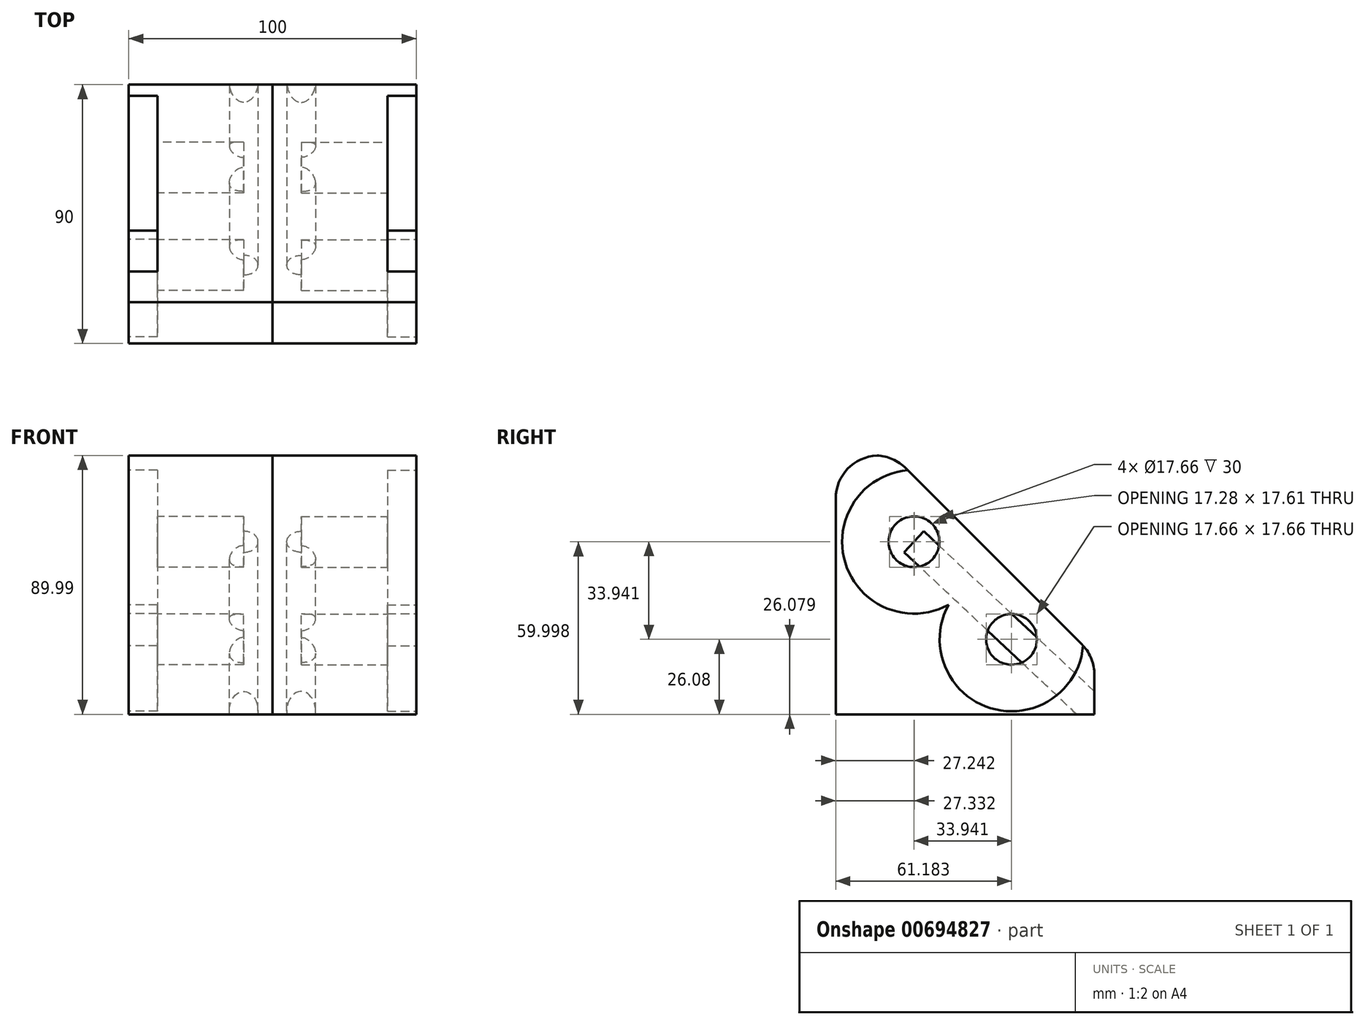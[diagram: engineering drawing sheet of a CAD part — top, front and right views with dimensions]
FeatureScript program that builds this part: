
annotation { "Feature Type Name" : "Feature", "Feature Type Description" : "" }
export const myFeature = defineFeature(function(context is Context, id is Id, definition is map)
    precondition{}
    {
        {
            var Q0;
            Q0=qCreatedBy(makeId("Right.planeOp"),FACE);
            var sketch = newSketch(context, id + "F0", { "sketchPlane" : qUnion([Q0])});
            skLineSegment(sketch, "E0.bottom", {"start": v(45, 45) * mm, "end": v(-45, 45) * mm});
            skLineSegment(sketch, "E0.top", {"start": v(45, -45) * mm, "end": v(-45, -45) * mm});
            skLineSegment(sketch, "E0.left", {"start": v(45, 45) * mm, "end": v(45, -45) * mm});
            skLineSegment(sketch, "E0.right", {"start": v(-45, 45) * mm, "end": v(-45, -45) * mm});
            skPoint(sketch, "E0.middle", {"position": v(0, 0) * mm});
            skCircle(sketch, "E1", {"center": v(-17.76, 15.02) * mm, "radius": 8.83 * mm});
            skCircle(sketch, "E2", {"center": v(16.18, -18.92) * mm, "radius": 8.83 * mm});
            skLineSegment(sketch, "E3", {"start": v(-17.76, 15.02) * mm, "end": v(-17.76, -18.92) * mm, "construction": true});
            skLineSegment(sketch, "E4", {"start": v(-17.76, -18.92) * mm, "end": v(16.18, -18.92) * mm, "construction": true});
            skLineSegment(sketch, "E5", {"start": v(-17.76, 15.02) * mm, "end": v(16.18, -18.92) * mm, "construction": true});
            skCircle(sketch, "E6", {"center": v(-17.76, 15.02) * mm, "radius": 25 * mm});
            skCircle(sketch, "E7", {"center": v(16.18, -18.92) * mm, "radius": 25 * mm});
            skSolve(sketch);
        }
        {
            var Q0;
            Q0=makeQuery(id+"F0.imprint","IMPRINT",FACE,{"disambiguationData":[TD([[makeQuery(id+"F0.imprint","IMPRINT",EDGE,{"derivedFrom":sQuery(id+"F0.wireOp",EDGE,"E0.bottom")}),1.0]])]});
            var Q1;
            Q1=makeQuery(id+"F0.imprint","IMPRINT",FACE,{"disambiguationData":[TD([[makeQuery(id+"F0.imprint","IMPRINT",EDGE,{"derivedFrom":sQuery(id+"F0.wireOp",EDGE,"E2")}),-1.0]])]});
            var Q2;
            Q2=makeQuery(id+"F0.imprint","IMPRINT",FACE,{"disambiguationData":[TD([[makeQuery(id+"F0.imprint","IMPRINT",EDGE,{"derivedFrom":sQuery(id+"F0.wireOp",EDGE,"E1")}),-1.0]])]});
            var Q3;
            {var subQ0=sQuery(id+"F0.wireOp",EDGE,"E7");var subQ1=sQuery(id+"F0.wireOp",EDGE,"E6");var subQ2=makeQuery(id+"F0.imprint","INTERSECT",VERTEX,{"disambiguationData":[OD(0.0)],"derivedFrom":[subQ1,subQ0]});Q3=makeQuery(id+"F0.imprint","IMPRINT",FACE,{"disambiguationData":[TD([[makeQuery(id+"F0.imprint","IMPRINT",EDGE,{"disambiguationData":[TD([[subQ2,-1.0]])],"derivedFrom":subQ1}),1.0]])]});}
            extrude(context, id + "F1", {"entities" : qUnion([Q0, Q1, Q2, Q3]), "depth" : 50 * mm, "offsetDistance" : 25 * mm});
        }
        {
            var Q0;
            Q0=makeQuery(id+"F1.opExtrude","SWEPT_EDGE",EDGE,{"disambiguationData":[OSD([sQuery(id+"F0.wireOp",EDGE,"E0.bottom"),sQuery(id+"F0.wireOp",EDGE,"E0.left")])]});
            chamfer(context, id + "F2", {"entities" : qUnion([Q0]), "width" : 70 * mm, "tangentPropagation" : true});
        }
        {
            var Q0;
            {var subQ0=sQuery(id+"F0.wireOp",EDGE,"E0.left");Q0=makeQuery(id+"F2.opChamfer","BLEND_EDGE",EDGE,{"blendedFrom":[makeQuery(id+"F1.opExtrude","SWEPT_EDGE",EDGE,{"disambiguationData":[OSD([sQuery(id+"F0.wireOp",EDGE,"E0.bottom"),subQ0])]}),makeQuery(id+"F1.opExtrude","SWEPT_FACE",FACE,{"disambiguationData":[OSD([subQ0])]})],"blendedInto":[makeQuery(id+"F1.opExtrude","SWEPT_FACE",FACE,{"disambiguationData":[OSD([subQ0])]})]});}
            var Q1;
            {var subQ0=sQuery(id+"F0.wireOp",EDGE,"E0.bottom");Q1=makeQuery(id+"F2.opChamfer","BLEND_EDGE",EDGE,{"blendedFrom":[makeQuery(id+"F1.opExtrude","SWEPT_EDGE",EDGE,{"disambiguationData":[OSD([subQ0,sQuery(id+"F0.wireOp",EDGE,"E0.left")])]}),makeQuery(id+"F1.opExtrude","SWEPT_FACE",FACE,{"disambiguationData":[OSD([subQ0])]})],"blendedInto":[makeQuery(id+"F1.opExtrude","SWEPT_FACE",FACE,{"disambiguationData":[OSD([subQ0])]})]});}
            var Q2;
            Q2=makeQuery(id+"F1.opExtrude","SWEPT_EDGE",EDGE,{"disambiguationData":[OSD([sQuery(id+"F0.wireOp",EDGE,"E0.bottom"),sQuery(id+"F0.wireOp",EDGE,"E0.right")])]});
            fillet(context, id + "F3", {"entities" : qUnion([Q0, Q1, Q2]), "radius" : 15 * mm, "tangentPropagation" : true, "allowEdgeOverflow" : false});
        }
        {
            var Q0;
            Q0=makeQuery(id+"F0.imprint","IMPRINT",FACE,{"disambiguationData":[TD([[makeQuery(id+"F0.imprint","IMPRINT",EDGE,{"derivedFrom":sQuery(id+"F0.wireOp",EDGE,"E1")}),-1.0]])]});
            var Q1;
            Q1=makeQuery(id+"F0.imprint","IMPRINT",FACE,{"disambiguationData":[TD([[makeQuery(id+"F0.imprint","IMPRINT",EDGE,{"derivedFrom":sQuery(id+"F0.wireOp",EDGE,"E2")}),-1.0]])]});
            var Q2;
            {var subQ0=sQuery(id+"F0.wireOp",EDGE,"E7");var subQ1=sQuery(id+"F0.wireOp",EDGE,"E6");var subQ2=makeQuery(id+"F0.imprint","INTERSECT",VERTEX,{"disambiguationData":[OD(0.0)],"derivedFrom":[subQ1,subQ0]});Q2=makeQuery(id+"F0.imprint","IMPRINT",FACE,{"disambiguationData":[TD([[makeQuery(id+"F0.imprint","IMPRINT",EDGE,{"disambiguationData":[TD([[subQ2,-1.0]])],"derivedFrom":subQ1}),1.0]])]});}
            extrude(context, id + "F4", {"entities" : qUnion([Q0, Q1, Q2]), "operationType" : NewBodyOperationType.REMOVE, "depth" : 10 * mm, "offsetDistance" : 25 * mm});
        }
        {
            var Q0;
            Q0=makeQuery(id+"F0.imprint","IMPRINT",FACE,{"disambiguationData":[TD([[makeQuery(id+"F0.imprint","IMPRINT",EDGE,{"derivedFrom":sQuery(id+"F0.wireOp",EDGE,"E0.bottom")}),1.0]])]});
            var sketch = newSketch(context, id + "F5", { "sketchPlane" : qUnion([Q0])});
            skPoint(sketch, "E8.0", {"position": v(10.58, 9.42) * mm});
            skArc(sketch, "E9.0.0", {"start": v(14.01, 5.99) * mm, "mid": v(8.93, 5) * mm, "end": v(4.16, 3) * mm});
            skArc(sketch, "E9.0.1", {"start": v(4.16, 3) * mm, "mid": v(6.17, 7.77) * mm, "end": v(7.15, 12.85) * mm});
            skLineSegment(sketch, "E9.0.2", {"start": v(7.15, 12.85) * mm, "end": v(14.01, 5.99) * mm});
            skSolve(sketch);
        }
        {
            var Q0;
            Q0 = qSketchRegion(id + "F5", true);
            var Q1;
            Q1=makeQuery(id+"F4.boolean.opBoolean","COPY",FACE,{"derivedFrom":makeQuery(id+"F4.opExtrude","CAP_FACE",FACE,{"disambiguationData":[OSD([sQuery(id+"F0.wireOp",EDGE,"E1"),sQuery(id+"F0.wireOp",EDGE,"E2"),sQuery(id+"F0.wireOp",EDGE,"E6"),sQuery(id+"F0.wireOp",EDGE,"E7")])],"isStart":false})});
            extrude(context, id + "F6", {"entities" : qUnion([Q0]), "operationType" : NewBodyOperationType.REMOVE, "endBound" : BoundingType.UP_TO_SURFACE, "depth" : 25 * mm, "endBoundEntityFace" : qUnion([Q1]), "offsetDistance" : 25 * mm});
        }
        {
            var Q0;
            Q0=makeQuery(id+"F1.opExtrude","CAP_FACE",FACE,{"disambiguationData":[OSD([sQuery(id+"F0.wireOp",EDGE,"E0.bottom"),sQuery(id+"F0.wireOp",EDGE,"E0.top"),sQuery(id+"F0.wireOp",EDGE,"E0.left"),sQuery(id+"F0.wireOp",EDGE,"E0.right"),sQuery(id+"F0.wireOp",EDGE,"E1"),sQuery(id+"F0.wireOp",EDGE,"E2")])],"isStart":false});
            var sketch = newSketch(context, id + "F7", { "sketchPlane" : qUnion([Q0])});
            skCircle(sketch, "E10.0", {"center": v(-17.76, 15.02) * mm, "radius": 8.83 * mm});
            skCircle(sketch, "E11.0", {"center": v(16.18, -18.92) * mm, "radius": 8.83 * mm});
            skSolve(sketch);
        }
        {
            var Q0;
            Q0 = qSketchRegion(id + "F7", true);
            extrude(context, id + "F8", {"entities" : qUnion([Q0]), "operationType" : NewBodyOperationType.ADD, "oppositeDirection" : true, "depth" : 10 * mm, "offsetDistance" : 25 * mm});
        }
        {
            var Q0;
            Q0=makeQuery(id+"F8.opExtrude","CAP_FACE",FACE,{"disambiguationData":[OSD([sQuery(id+"F7.wireOp",EDGE,"E10.0")])],"isStart":false});
            var sketch = newSketch(context, id + "F9", { "sketchPlane" : qUnion([Q0])});
            skCircle(sketch, "E12.0.0", {"center": v(17.76, 15.02) * mm, "radius": 8.83 * mm});
            skCircle(sketch, "E13.0.0", {"center": v(-16.18, -18.92) * mm, "radius": 8.83 * mm});
            skLineSegment(sketch, "E14", {"start": v(11.51, 8.78) * mm, "end": v(5.65, 15.02) * mm});
            skLineSegment(sketch, "E15", {"start": v(17.76, 15.02) * mm, "end": v(-52.17, -50.63) * mm});
            skSolve(sketch);
        }
        {
            var Q0;
            Q0=sQuery(id+"F9.wireOp",EDGE,"E14");
            cPlane(context, id + "F10", {"entities" : qUnion([Q0]), "cplaneType" : CPlaneType.LINE_ANGLE, "offset" : 25 * mm, "angle" : 0 * degree, "width" : 150 * mm, "height" : 150 * mm});
        }
        {
            var Q0;
            Q0=qCreatedBy(id+"F10.planeOp",FACE);
            var sketch = newSketch(context, id + "F11", { "sketchPlane" : qUnion([Q0])});
            skLineSegment(sketch, "E16.0", {"start": v(40, -10.03) * mm, "end": v(40, 7.63) * mm});
            skCircle(sketch, "E17", {"center": v(40, -1.2) * mm, "radius": 5 * mm});
            skSolve(sketch);
        }
        {
            var Q0;
            {var subQ0=sQuery(id+"F11.wireOp",EDGE,"E17");var subQ1=sQuery(id+"F11.wireOp",EDGE,"E16.0");var subQ2=makeQuery(id+"F11.imprint","INTERSECT",VERTEX,{"disambiguationData":[OD(0.0)],"derivedFrom":[subQ1,subQ0]});Q0=makeQuery(id+"F11.imprint","IMPRINT",FACE,{"disambiguationData":[TD([[makeQuery(id+"F11.imprint","IMPRINT",EDGE,{"disambiguationData":[TD([[subQ2,-1.0]])],"derivedFrom":subQ1}),1.0]])]});}
            var Q1;
            {var subQ0=sQuery(id+"F11.wireOp",EDGE,"E17");var subQ1=sQuery(id+"F11.wireOp",EDGE,"E16.0");var subQ2=makeQuery(id+"F11.imprint","INTERSECT",VERTEX,{"disambiguationData":[OD(0.0)],"derivedFrom":[subQ1,subQ0]});Q1=makeQuery(id+"F11.imprint","IMPRINT",FACE,{"disambiguationData":[TD([[makeQuery(id+"F11.imprint","IMPRINT",EDGE,{"disambiguationData":[TD([[subQ2,-1.0]])],"derivedFrom":subQ1}),-1.0]])]});}
            var Q2;
            Q2=sQuery(id+"F9.wireOp",EDGE,"E15");
            sweep(context, id + "F12", {"operationType" : NewBodyOperationType.REMOVE, "profiles" : qUnion([Q0, Q1]), "path" : qUnion([Q2])});
        }
        {
            var Q0;
            Q0=makeQuery(id+"F1.opExtrude","SWEPT_BODY",BODY,{"disambiguationData":[OSD([sQuery(id+"F0.wireOp",EDGE,"E0.bottom"),sQuery(id+"F0.wireOp",EDGE,"E0.top"),sQuery(id+"F0.wireOp",EDGE,"E0.left"),sQuery(id+"F0.wireOp",EDGE,"E0.right"),sQuery(id+"F0.wireOp",EDGE,"E1"),sQuery(id+"F0.wireOp",EDGE,"E2")])]});
            var Q1;
            Q1=makeQuery(id+"F8.boolean.opBoolean","MERGE",FACE,{"derivedFrom":[makeQuery(id+"F1.opExtrude","CAP_FACE",FACE,{"disambiguationData":[OSD([sQuery(id+"F0.wireOp",EDGE,"E0.bottom"),sQuery(id+"F0.wireOp",EDGE,"E0.top"),sQuery(id+"F0.wireOp",EDGE,"E0.left"),sQuery(id+"F0.wireOp",EDGE,"E0.right"),sQuery(id+"F0.wireOp",EDGE,"E1"),sQuery(id+"F0.wireOp",EDGE,"E2")])],"isStart":false}),makeQuery(id+"F8.opExtrude","CAP_FACE",FACE,{"disambiguationData":[OSD([sQuery(id+"F7.wireOp",EDGE,"E10.0")])],"isStart":true}),makeQuery(id+"F8.opExtrude","CAP_FACE",FACE,{"disambiguationData":[OSD([sQuery(id+"F7.wireOp",EDGE,"E11.0")])],"isStart":true})]});
            mirror(context, id + "F13", {"entities" : qUnion([Q0]), "mirrorPlane" : qUnion([Q1])});
        }
    });
